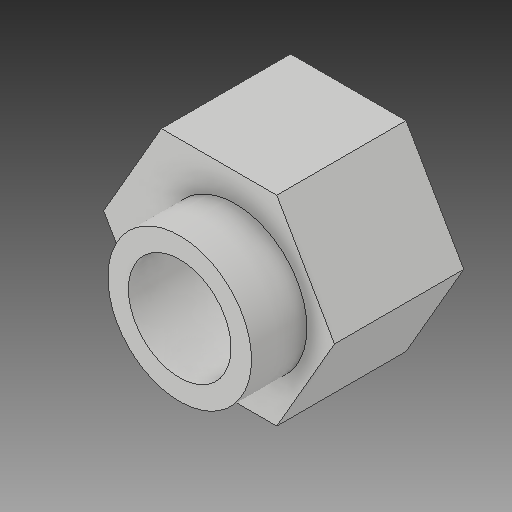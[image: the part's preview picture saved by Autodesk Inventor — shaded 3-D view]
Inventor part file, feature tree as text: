
AUTODESK INVENTOR PART (.ipt)
format: ipt  version: 2018 (Build 220112000, 112)  size: 121,344 bytes
history: native  units: mm
features: other x3, sketch x3
ambient origin geometry x8: Origin, YZ Plane, XZ Plane, XY Plane, X Axis, Y Axis, Z Axis, Center Point
bodies: Solid1 (feature_tree)
feature tree (6):
  other  "Eccentric Spacer_MIR.ipt"
  other  "Solid1::Eccentric Spacer_MIR.ipt"
  other  "TaggingFeature1"
  sketch  "Sketch1"  dims[d0=10.0mm]
  sketch  "Sketch2"
  sketch  "Sketch3"
